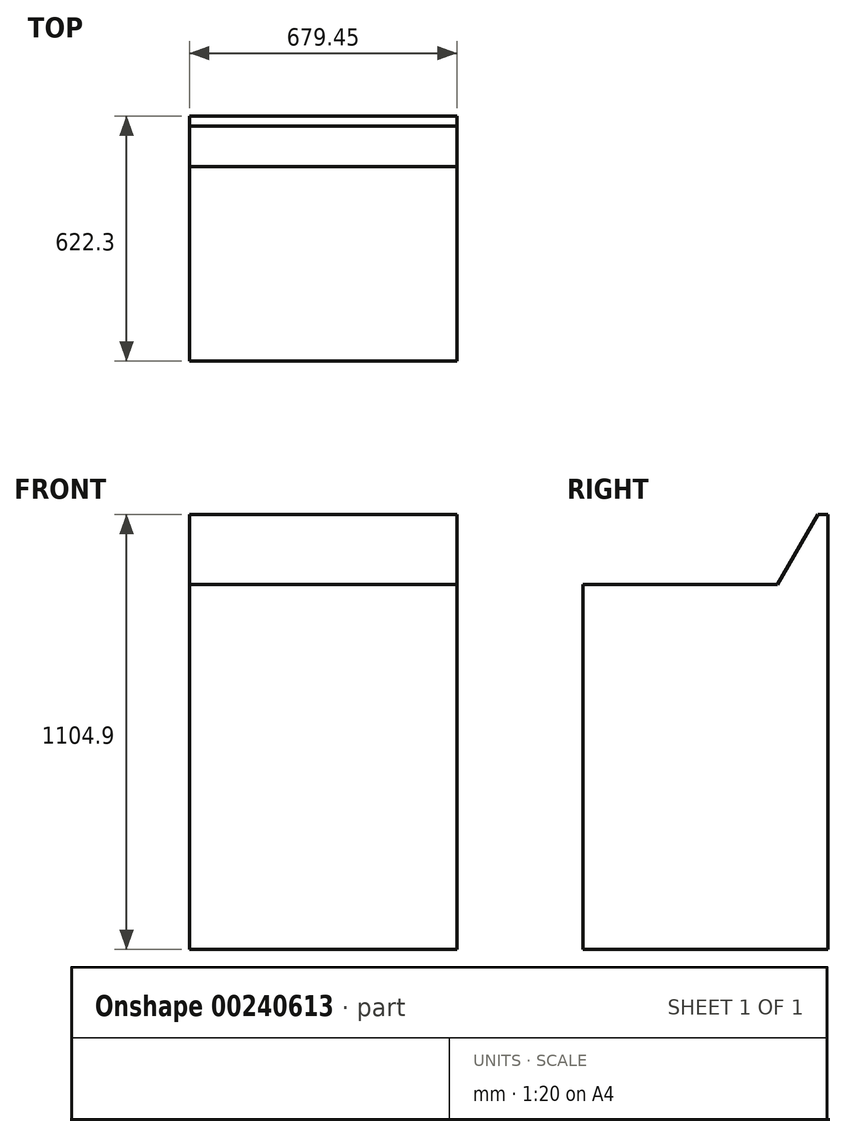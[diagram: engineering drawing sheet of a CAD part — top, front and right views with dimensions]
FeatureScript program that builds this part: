
annotation { "Feature Type Name" : "Feature", "Feature Type Description" : "" }
export const myFeature = defineFeature(function(context is Context, id is Id, definition is map)
    precondition{}
    {
        {
            var Q0;
            Q0=qCreatedBy(makeId("Top.planeOp"),FACE);
            var sketch = newSketch(context, id + "F0", { "sketchPlane" : qUnion([Q0])});
            skLineSegment(sketch, "E0.bottom", {"start": v(-335.8, 369.13) * mm, "end": v(343.65, 369.13) * mm});
            skLineSegment(sketch, "E0.top", {"start": v(-335.8, -253.17) * mm, "end": v(343.65, -253.17) * mm});
            skLineSegment(sketch, "E0.left", {"start": v(-335.8, 369.13) * mm, "end": v(-335.8, -253.17) * mm});
            skLineSegment(sketch, "E0.right", {"start": v(343.65, 369.13) * mm, "end": v(343.65, -253.17) * mm});
            skSolve(sketch);
        }
        {
            var Q0;
            Q0=makeQuery(id+"F0.imprint","IMPRINT",FACE,{"disambiguationData":[TD([[makeQuery(id+"F0.imprint","IMPRINT",EDGE,{"derivedFrom":sQuery(id+"F0.wireOp",EDGE,"E0.bottom")}),-1.0]])]});
            extrude(context, id + "F1", {"entities" : qUnion([Q0]), "depth" : 927.1 * mm, "offsetDistance" : 25.4 * mm});
        }
        {
            var Q0;
            Q0=makeQuery(id+"F1.opExtrude","SWEPT_FACE",FACE,{"disambiguationData":[OSD([sQuery(id+"F0.wireOp",EDGE,"E0.left")])]});
            var sketch = newSketch(context, id + "F2", { "sketchPlane" : qUnion([Q0])});
            skLineSegment(sketch, "E1", {"start": v(-369.13, 927.1) * mm, "end": v(-369.13, 1104.9) * mm});
            skLineSegment(sketch, "E2", {"start": v(-369.13, 1104.9) * mm, "end": v(-343.73, 1104.9) * mm});
            skLineSegment(sketch, "E3", {"start": v(-343.73, 1104.9) * mm, "end": v(-241.08, 927.1) * mm});
            skLineSegment(sketch, "E4", {"start": v(-241.08, 927.1) * mm, "end": v(-369.13, 927.1) * mm});
            skSolve(sketch);
        }
        {
            var Q0;
            Q0=makeQuery(id+"F2.imprint","IMPRINT",FACE,{"disambiguationData":[TD([[makeQuery(id+"F2.imprint","IMPRINT",EDGE,{"derivedFrom":sQuery(id+"F2.wireOp",EDGE,"E1")}),-1.0]])]});
            var Q1;
            Q1=makeQuery(id+"F1.opExtrude","SWEPT_FACE",FACE,{"disambiguationData":[OSD([sQuery(id+"F0.wireOp",EDGE,"E0.right")])]});
            extrude(context, id + "F3", {"entities" : qUnion([Q0]), "operationType" : NewBodyOperationType.ADD, "endBound" : BoundingType.UP_TO_SURFACE, "oppositeDirection" : true, "depth" : 256.54 * mm, "endBoundEntityFace" : qUnion([Q1]), "offsetDistance" : 25.4 * mm});
        }
    });
